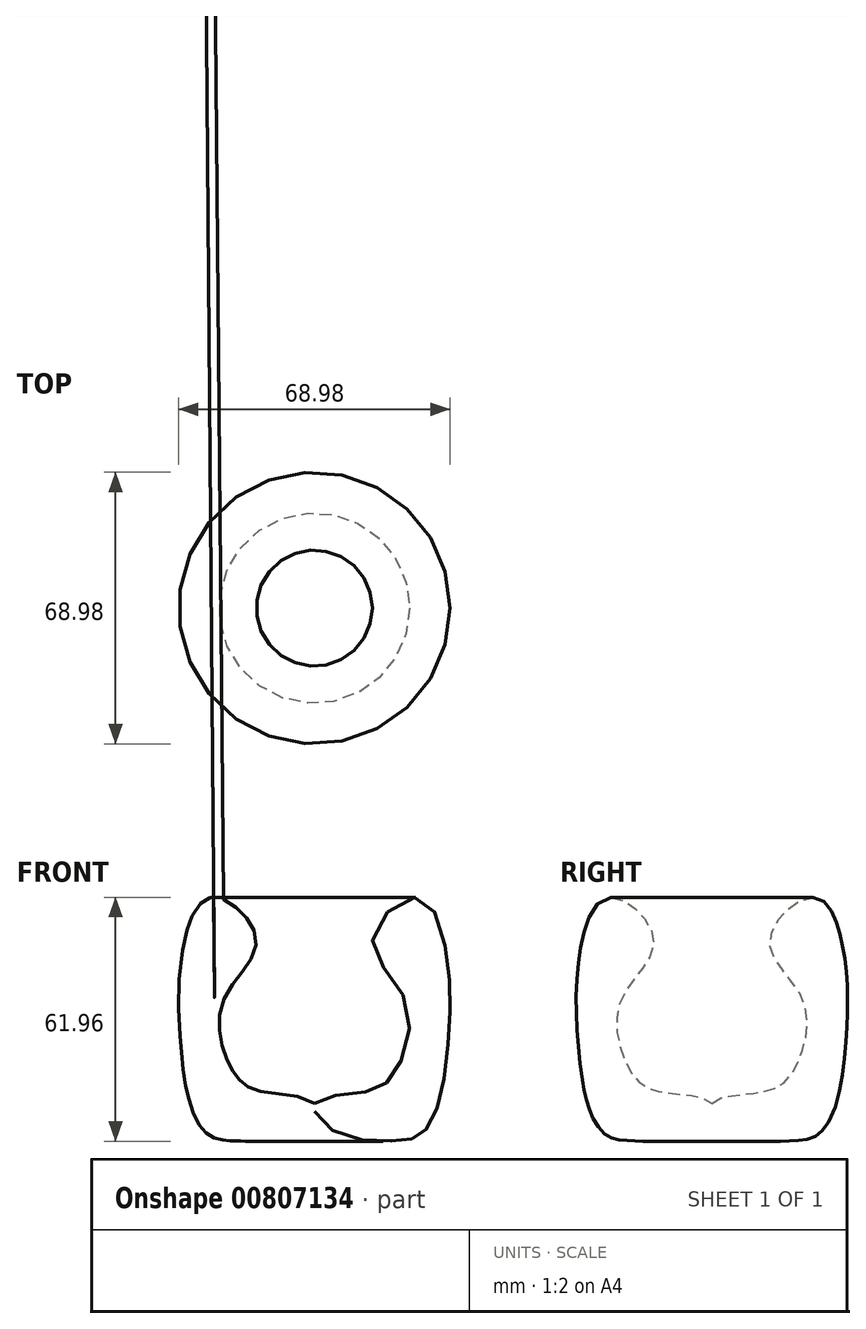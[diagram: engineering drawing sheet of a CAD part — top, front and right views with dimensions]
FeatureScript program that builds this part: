
annotation { "Feature Type Name" : "Feature", "Feature Type Description" : "" }
export const myFeature = defineFeature(function(context is Context, id is Id, definition is map)
    precondition{}
    {
        {
            var Q0;
            Q0=qCreatedBy(makeId("Front.planeOp"),FACE);
            var sketch = newSketch(context, id + "F0", { "sketchPlane" : qUnion([Q0])});
            skLineSegment(sketch, "E0", {"start": v(0, 75.42) * mm, "end": v(0, -74.28) * mm});
            skFitSpline(sketch, "E1", {"points": [v(20.75, -22.18) * mm, v(5.3, -19.9) * mm, v(0, -12.74) * mm, v(12.16, -9.88) * mm, v(20.18, -5.3) * mm, v(23.33, 13.02) * mm, v(14.74, 28.77) * mm, v(26.2, 39.64) * mm, v(33.63, 25.05) * mm, v(34.2, 5.87) * mm, v(31.34, -13.6) * mm, v(26.76, -20.75) * mm, v(20.75, -22.18) * mm]});
            skSolve(sketch);
        }
        {
            var Q0;
            {var subQ0=sQuery(id+"F0.wireOp",EDGE,"E1");var subQ1=sQuery(id+"F0.wireOp",EDGE,"E0");var subQ2=makeQuery(id+"F0.imprint","INTERSECT",VERTEX,{"disambiguationData":[OD(0.0)],"derivedFrom":[subQ1,subQ0]});Q0=makeQuery(id+"F0.imprint","IMPRINT",FACE,{"disambiguationData":[TD([[makeQuery(id+"F0.imprint","IMPRINT",EDGE,{"disambiguationData":[TD([[subQ2,1.0]])],"derivedFrom":subQ1}),1.0]])]});}
            var Q1;
            Q1=sQuery(id+"F0.wireOp",EDGE,"E0");
            revolve(context, id + "F1", {"surfaceOperationType" : NewSurfaceOperationType.NEW, "entities" : qUnion([Q0]), "axis" : qUnion([Q1]), "revolveType" : RevolveType.FULL});
        }
    });
